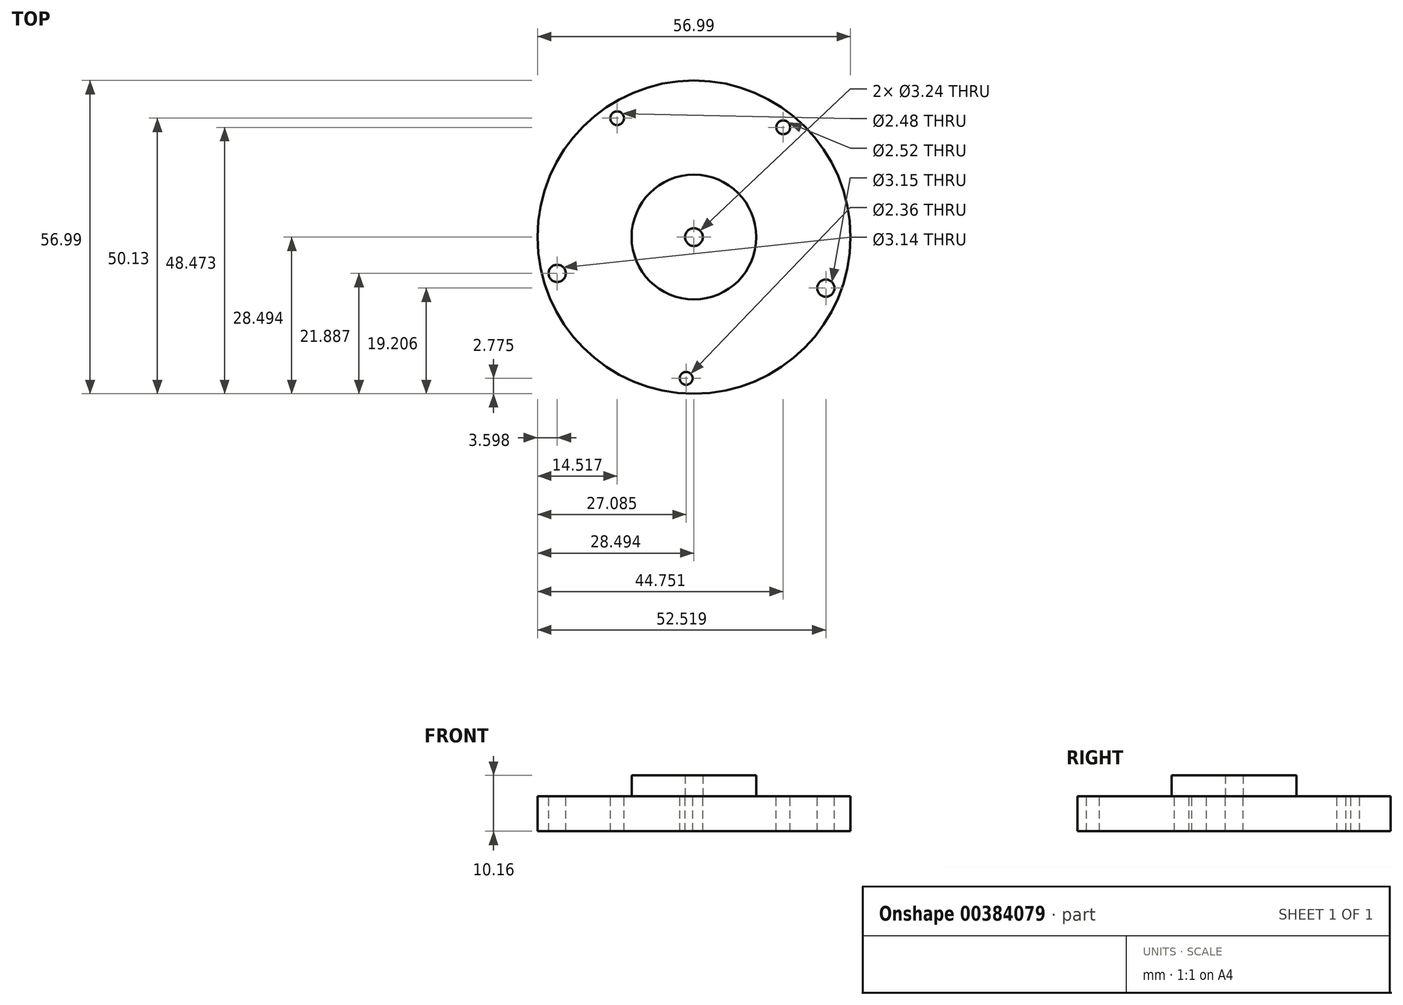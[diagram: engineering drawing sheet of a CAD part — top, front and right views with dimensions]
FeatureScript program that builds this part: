
annotation { "Feature Type Name" : "Feature", "Feature Type Description" : "" }
export const myFeature = defineFeature(function(context is Context, id is Id, definition is map)
    precondition{}
    {
        {
            var Q0;
            Q0=qCreatedBy(makeId("Top.planeOp"),FACE);
            var sketch = newSketch(context, id + "F0", { "sketchPlane" : qUnion([Q0])});
            skCircle(sketch, "E0", {"center": v(-19.83, 14.42) * mm, "radius": 28.5 * mm});
            skCircle(sketch, "E1", {"center": v(-19.83, 14.42) * mm, "radius": 11.35 * mm});
            skCircle(sketch, "E2", {"center": v(-19.83, 14.42) * mm, "radius": 1.62 * mm});
            skCircle(sketch, "E3.cCircle", {"center": v(-19.83, 14.42) * mm, "radius": 20.84 * mm, "construction": true});
            skLineSegment(sketch, "E3.0", {"start": v(-44.72, 7.82) * mm, "end": v(-33.8, 36.06) * mm, "construction": true});
            skLineSegment(sketch, "E3.1", {"start": v(-33.8, 36.06) * mm, "end": v(-3.57, 34.4) * mm, "construction": true});
            skLineSegment(sketch, "E3.2", {"start": v(-3.57, 34.4) * mm, "end": v(4.2, 5.14) * mm, "construction": true});
            skLineSegment(sketch, "E3.3", {"start": v(4.2, 5.14) * mm, "end": v(-21.24, -11.3) * mm, "construction": true});
            skLineSegment(sketch, "E3.4", {"start": v(-21.24, -11.3) * mm, "end": v(-44.72, 7.82) * mm, "construction": true});
            skPoint(sketch, "E3.0.midPoint", {"position": v(-39.26, 21.94) * mm});
            skCircle(sketch, "E4", {"center": v(-33.8, 36.06) * mm, "radius": 1.24 * mm});
            skCircle(sketch, "E5", {"center": v(-3.57, 34.4) * mm, "radius": 1.26 * mm});
            skCircle(sketch, "E6", {"center": v(4.2, 5.14) * mm, "radius": 1.58 * mm});
            skCircle(sketch, "E7", {"center": v(-21.24, -11.3) * mm, "radius": 1.18 * mm});
            skCircle(sketch, "E8", {"center": v(-44.72, 7.82) * mm, "radius": 1.57 * mm});
            skSolve(sketch);
        }
        {
            var Q0;
            Q0=makeQuery(id+"F0.imprint","IMPRINT",FACE,{"disambiguationData":[TD([[makeQuery(id+"F0.imprint","IMPRINT",EDGE,{"derivedFrom":sQuery(id+"F0.wireOp",EDGE,"E0")}),1.0]])]});
            var Q1;
            Q1=makeQuery(id+"F0.imprint","IMPRINT",FACE,{"disambiguationData":[TD([[makeQuery(id+"F0.imprint","IMPRINT",EDGE,{"derivedFrom":sQuery(id+"F0.wireOp",EDGE,"E1")}),1.0]])]});
            extrude(context, id + "F1", {"entities" : qUnion([Q0, Q1]), "oppositeDirection" : true, "depth" : 6.35 * mm});
        }
        {
            var Q0;
            Q0=makeQuery(id+"F0.imprint","IMPRINT",FACE,{"disambiguationData":[TD([[makeQuery(id+"F0.imprint","IMPRINT",EDGE,{"derivedFrom":sQuery(id+"F0.wireOp",EDGE,"E1")}),1.0]])]});
            extrude(context, id + "F2", {"entities" : qUnion([Q0]), "depth" : 3.8 * mm});
        }
    });
